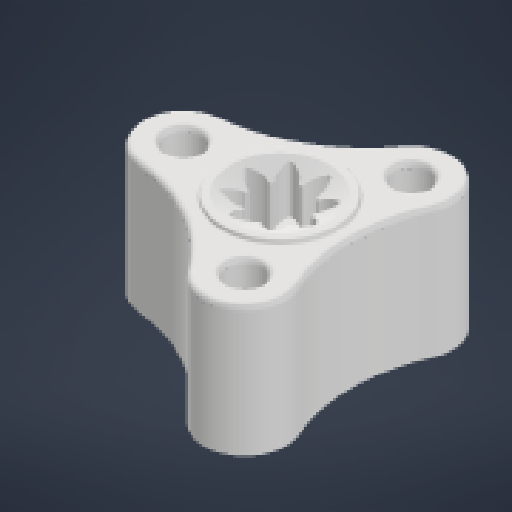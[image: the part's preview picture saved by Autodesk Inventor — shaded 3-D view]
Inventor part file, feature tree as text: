
AUTODESK INVENTOR PART (.ipt)
format: ipt  version: 2024 (Build 280153000, 153)  size: 370,688 bytes
history: native  units: in
note: dims shown in document units (in); Inventor stores cm internally (conversion verified against a paired STEP export)
features: extrude x1, sketch x1
ambient origin geometry x8: Origin, YZ Plane, XZ Plane, XY Plane, X Axis, Y Axis, Z Axis, Center Point
bodies: Solid2 (feature_tree), Solid1 (feature_tree)
feature tree (2):
  extrude  "Extrusion1"  [1 undecoded]
  sketch  "Sketch2"  dims[d0=0.2in d1=0.05in d2=0.0in d3=0.0in]
note: 1 required parameter value undecoded (feature->parameter linkage not recoverable at this tier; creation-order binding heuristic only, values carry confidence <= 0.55)
